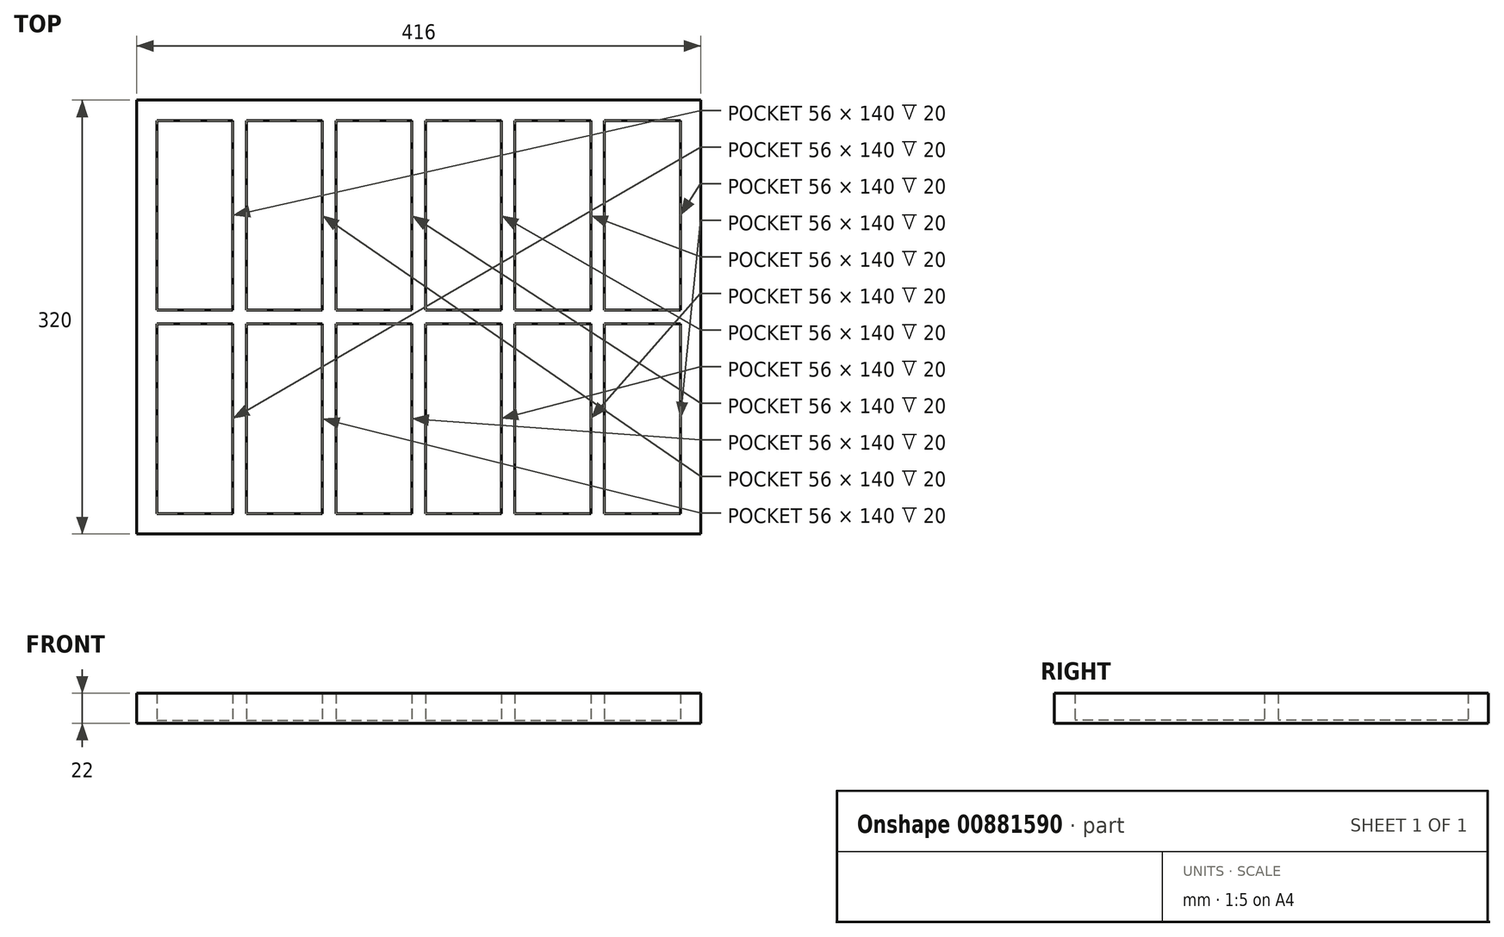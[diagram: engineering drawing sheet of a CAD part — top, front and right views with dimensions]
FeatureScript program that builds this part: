
annotation { "Feature Type Name" : "Feature", "Feature Type Description" : "" }
export const myFeature = defineFeature(function(context is Context, id is Id, definition is map)
    precondition{}
    {
        {
            var Q0;
            Q0=qCreatedBy(makeId("Top.planeOp"),FACE);
            var sketch = newSketch(context, id + "F0", { "sketchPlane" : qUnion([Q0])});
            skLineSegment(sketch, "E0.bottom", {"start": v(-136.96, -38.71) * mm, "end": v(-80.96, -38.71) * mm});
            skLineSegment(sketch, "E0.top", {"start": v(-136.96, -178.71) * mm, "end": v(-80.96, -178.71) * mm});
            skLineSegment(sketch, "E0.left", {"start": v(-136.96, -38.71) * mm, "end": v(-136.96, -178.71) * mm});
            skLineSegment(sketch, "E0.right", {"start": v(-80.96, -38.71) * mm, "end": v(-80.96, -178.71) * mm});
            skLineSegment(sketch, "E1.0.1.0", {"start": v(-80.96, 111.29) * mm, "end": v(-80.96, -28.71) * mm});
            skLineSegment(sketch, "E1.0.1.1", {"start": v(-136.96, 111.29) * mm, "end": v(-80.96, 111.29) * mm});
            skLineSegment(sketch, "E1.0.1.2", {"start": v(-136.96, 111.29) * mm, "end": v(-136.96, -28.71) * mm});
            skLineSegment(sketch, "E1.0.1.3", {"start": v(-136.96, -28.71) * mm, "end": v(-80.96, -28.71) * mm});
            skLineSegment(sketch, "E1.1.0.0", {"start": v(-14.96, -38.71) * mm, "end": v(-14.96, -178.71) * mm});
            skLineSegment(sketch, "E1.1.0.1", {"start": v(-70.96, -38.71) * mm, "end": v(-14.96, -38.71) * mm});
            skLineSegment(sketch, "E1.1.0.2", {"start": v(-70.96, -38.71) * mm, "end": v(-70.96, -178.71) * mm});
            skLineSegment(sketch, "E1.1.0.3", {"start": v(-70.96, -178.71) * mm, "end": v(-14.96, -178.71) * mm});
            skLineSegment(sketch, "E1.1.1.0", {"start": v(-14.96, 111.29) * mm, "end": v(-14.96, -28.71) * mm});
            skLineSegment(sketch, "E1.1.1.1", {"start": v(-70.96, 111.29) * mm, "end": v(-14.96, 111.29) * mm});
            skLineSegment(sketch, "E1.1.1.2", {"start": v(-70.96, 111.29) * mm, "end": v(-70.96, -28.71) * mm});
            skLineSegment(sketch, "E1.1.1.3", {"start": v(-70.96, -28.71) * mm, "end": v(-14.96, -28.71) * mm});
            skLineSegment(sketch, "E1.2.0.0", {"start": v(51.04, -38.71) * mm, "end": v(51.04, -178.71) * mm});
            skLineSegment(sketch, "E1.2.0.1", {"start": v(-4.96, -38.71) * mm, "end": v(51.04, -38.71) * mm});
            skLineSegment(sketch, "E1.2.0.2", {"start": v(-4.96, -38.71) * mm, "end": v(-4.96, -178.71) * mm});
            skLineSegment(sketch, "E1.2.0.3", {"start": v(-4.96, -178.71) * mm, "end": v(51.04, -178.71) * mm});
            skLineSegment(sketch, "E1.2.1.0", {"start": v(51.04, 111.29) * mm, "end": v(51.04, -28.71) * mm});
            skLineSegment(sketch, "E1.2.1.1", {"start": v(-4.96, 111.29) * mm, "end": v(51.04, 111.29) * mm});
            skLineSegment(sketch, "E1.2.1.2", {"start": v(-4.96, 111.29) * mm, "end": v(-4.96, -28.71) * mm});
            skLineSegment(sketch, "E1.2.1.3", {"start": v(-4.96, -28.71) * mm, "end": v(51.04, -28.71) * mm});
            skLineSegment(sketch, "E1.3.0.0", {"start": v(117.04, -38.71) * mm, "end": v(117.04, -178.71) * mm});
            skLineSegment(sketch, "E1.3.0.1", {"start": v(61.04, -38.71) * mm, "end": v(117.04, -38.71) * mm});
            skLineSegment(sketch, "E1.3.0.2", {"start": v(61.04, -38.71) * mm, "end": v(61.04, -178.71) * mm});
            skLineSegment(sketch, "E1.3.0.3", {"start": v(61.04, -178.71) * mm, "end": v(117.04, -178.71) * mm});
            skLineSegment(sketch, "E1.3.1.0", {"start": v(117.04, 111.29) * mm, "end": v(117.04, -28.71) * mm});
            skLineSegment(sketch, "E1.3.1.1", {"start": v(61.04, 111.29) * mm, "end": v(117.04, 111.29) * mm});
            skLineSegment(sketch, "E1.3.1.2", {"start": v(61.04, 111.29) * mm, "end": v(61.04, -28.71) * mm});
            skLineSegment(sketch, "E1.3.1.3", {"start": v(61.04, -28.71) * mm, "end": v(117.04, -28.71) * mm});
            skLineSegment(sketch, "E1.4.0.0", {"start": v(183.04, -38.71) * mm, "end": v(183.04, -178.71) * mm});
            skLineSegment(sketch, "E1.4.0.1", {"start": v(127.04, -38.71) * mm, "end": v(183.04, -38.71) * mm});
            skLineSegment(sketch, "E1.4.0.2", {"start": v(127.04, -38.71) * mm, "end": v(127.04, -178.71) * mm});
            skLineSegment(sketch, "E1.4.0.3", {"start": v(127.04, -178.71) * mm, "end": v(183.04, -178.71) * mm});
            skLineSegment(sketch, "E1.4.1.0", {"start": v(183.04, 111.29) * mm, "end": v(183.04, -28.71) * mm});
            skLineSegment(sketch, "E1.4.1.1", {"start": v(127.04, 111.29) * mm, "end": v(183.04, 111.29) * mm});
            skLineSegment(sketch, "E1.4.1.2", {"start": v(127.04, 111.29) * mm, "end": v(127.04, -28.71) * mm});
            skLineSegment(sketch, "E1.4.1.3", {"start": v(127.04, -28.71) * mm, "end": v(183.04, -28.71) * mm});
            skLineSegment(sketch, "E1.5.0.0", {"start": v(249.04, -38.71) * mm, "end": v(249.04, -178.71) * mm});
            skLineSegment(sketch, "E1.5.0.1", {"start": v(193.04, -38.71) * mm, "end": v(249.04, -38.71) * mm});
            skLineSegment(sketch, "E1.5.0.2", {"start": v(193.04, -38.71) * mm, "end": v(193.04, -178.71) * mm});
            skLineSegment(sketch, "E1.5.0.3", {"start": v(193.04, -178.71) * mm, "end": v(249.04, -178.71) * mm});
            skLineSegment(sketch, "E1.5.1.0", {"start": v(249.04, 111.29) * mm, "end": v(249.04, -28.71) * mm});
            skLineSegment(sketch, "E1.5.1.1", {"start": v(193.04, 111.29) * mm, "end": v(249.04, 111.29) * mm});
            skLineSegment(sketch, "E1.5.1.2", {"start": v(193.04, 111.29) * mm, "end": v(193.04, -28.71) * mm});
            skLineSegment(sketch, "E1.5.1.3", {"start": v(193.04, -28.71) * mm, "end": v(249.04, -28.71) * mm});
            skLineSegment(sketch, "E1.direction1", {"start": v(-80.96, -178.71) * mm, "end": v(-14.96, -178.71) * mm, "construction": true});
            skLineSegment(sketch, "E1.direction2", {"start": v(-80.96, -178.71) * mm, "end": v(-80.96, -28.71) * mm, "construction": true});
            skLineSegment(sketch, "E2.bottom", {"start": v(-151.96, 126.29) * mm, "end": v(264.04, 126.29) * mm});
            skLineSegment(sketch, "E2.top", {"start": v(-151.96, -193.71) * mm, "end": v(264.04, -193.71) * mm});
            skLineSegment(sketch, "E2.left", {"start": v(-151.96, 126.29) * mm, "end": v(-151.96, -193.71) * mm});
            skLineSegment(sketch, "E2.right", {"start": v(264.04, 126.29) * mm, "end": v(264.04, -193.71) * mm});
            skLineSegment(sketch, "E3", {"start": v(-136.96, 91.51) * mm, "end": v(-151.96, 91.51) * mm, "construction": true});
            skLineSegment(sketch, "E4", {"start": v(264.04, 95.62) * mm, "end": v(249.04, 95.62) * mm, "construction": true});
            skLineSegment(sketch, "E5", {"start": v(236.73, 111.29) * mm, "end": v(236.73, 126.29) * mm, "construction": true});
            skLineSegment(sketch, "E6", {"start": v(240.38, -178.71) * mm, "end": v(240.38, -193.71) * mm, "construction": true});
            skSolve(sketch);
        }
        {
            var Q0;
            Q0 = qSketchRegion(id + "F0", true);
            extrude(context, id + "F1", {"entities" : qUnion([Q0]), "depth" : 20 * mm, "offsetDistance" : 25 * mm});
        }
        {
            var Q0;
            Q0=makeQuery(id+"F1.opExtrude","CAP_FACE",FACE,{"disambiguationData":[OSD([sQuery(id+"F0.wireOp",EDGE,"E0.bottom"),sQuery(id+"F0.wireOp",EDGE,"E0.top"),sQuery(id+"F0.wireOp",EDGE,"E0.left"),sQuery(id+"F0.wireOp",EDGE,"E0.right"),sQuery(id+"F0.wireOp",EDGE,"E1.0.1.0"),sQuery(id+"F0.wireOp",EDGE,"E1.0.1.1"),sQuery(id+"F0.wireOp",EDGE,"E1.0.1.2"),sQuery(id+"F0.wireOp",EDGE,"E1.0.1.3"),sQuery(id+"F0.wireOp",EDGE,"E1.1.0.0"),sQuery(id+"F0.wireOp",EDGE,"E1.1.0.1"),sQuery(id+"F0.wireOp",EDGE,"E1.1.0.2"),sQuery(id+"F0.wireOp",EDGE,"E1.1.0.3"),sQuery(id+"F0.wireOp",EDGE,"E1.1.1.0"),sQuery(id+"F0.wireOp",EDGE,"E1.1.1.1"),sQuery(id+"F0.wireOp",EDGE,"E1.1.1.2"),sQuery(id+"F0.wireOp",EDGE,"E1.1.1.3"),sQuery(id+"F0.wireOp",EDGE,"E1.2.0.0"),sQuery(id+"F0.wireOp",EDGE,"E1.2.0.1"),sQuery(id+"F0.wireOp",EDGE,"E1.2.0.2"),sQuery(id+"F0.wireOp",EDGE,"E1.2.0.3"),sQuery(id+"F0.wireOp",EDGE,"E1.2.1.0"),sQuery(id+"F0.wireOp",EDGE,"E1.2.1.1"),sQuery(id+"F0.wireOp",EDGE,"E1.2.1.2"),sQuery(id+"F0.wireOp",EDGE,"E1.2.1.3"),sQuery(id+"F0.wireOp",EDGE,"E1.3.0.0"),sQuery(id+"F0.wireOp",EDGE,"E1.3.0.1"),sQuery(id+"F0.wireOp",EDGE,"E1.3.0.2"),sQuery(id+"F0.wireOp",EDGE,"E1.3.0.3"),sQuery(id+"F0.wireOp",EDGE,"E1.3.1.0"),sQuery(id+"F0.wireOp",EDGE,"E1.3.1.1"),sQuery(id+"F0.wireOp",EDGE,"E1.3.1.2"),sQuery(id+"F0.wireOp",EDGE,"E1.3.1.3"),sQuery(id+"F0.wireOp",EDGE,"E1.4.0.0"),sQuery(id+"F0.wireOp",EDGE,"E1.4.0.1"),sQuery(id+"F0.wireOp",EDGE,"E1.4.0.2"),sQuery(id+"F0.wireOp",EDGE,"E1.4.0.3"),sQuery(id+"F0.wireOp",EDGE,"E1.4.1.0"),sQuery(id+"F0.wireOp",EDGE,"E1.4.1.1"),sQuery(id+"F0.wireOp",EDGE,"E1.4.1.2"),sQuery(id+"F0.wireOp",EDGE,"E1.4.1.3"),sQuery(id+"F0.wireOp",EDGE,"E1.5.0.0"),sQuery(id+"F0.wireOp",EDGE,"E1.5.0.1"),sQuery(id+"F0.wireOp",EDGE,"E1.5.0.2"),sQuery(id+"F0.wireOp",EDGE,"E1.5.0.3"),sQuery(id+"F0.wireOp",EDGE,"E1.5.1.0"),sQuery(id+"F0.wireOp",EDGE,"E1.5.1.1"),sQuery(id+"F0.wireOp",EDGE,"E1.5.1.2"),sQuery(id+"F0.wireOp",EDGE,"E1.5.1.3"),sQuery(id+"F0.wireOp",EDGE,"E2.bottom"),sQuery(id+"F0.wireOp",EDGE,"E2.top"),sQuery(id+"F0.wireOp",EDGE,"E2.left"),sQuery(id+"F0.wireOp",EDGE,"E2.right")])],"isStart":true});
            var sketch = newSketch(context, id + "F2", { "sketchPlane" : qUnion([Q0])});
            skLineSegment(sketch, "E7.bottom", {"start": v(-151.96, 193.71) * mm, "end": v(264.04, 193.71) * mm});
            skLineSegment(sketch, "E7.top", {"start": v(-151.96, -126.29) * mm, "end": v(264.04, -126.29) * mm});
            skLineSegment(sketch, "E7.left", {"start": v(-151.96, 193.71) * mm, "end": v(-151.96, -126.29) * mm});
            skLineSegment(sketch, "E7.right", {"start": v(264.04, 193.71) * mm, "end": v(264.04, -126.29) * mm});
            skSolve(sketch);
        }
        {
            var Q0;
            Q0 = qSketchRegion(id + "F2", true);
            extrude(context, id + "F3", {"entities" : qUnion([Q0]), "operationType" : NewBodyOperationType.ADD, "depth" : 2 * mm, "offsetDistance" : 25 * mm});
        }
    });
